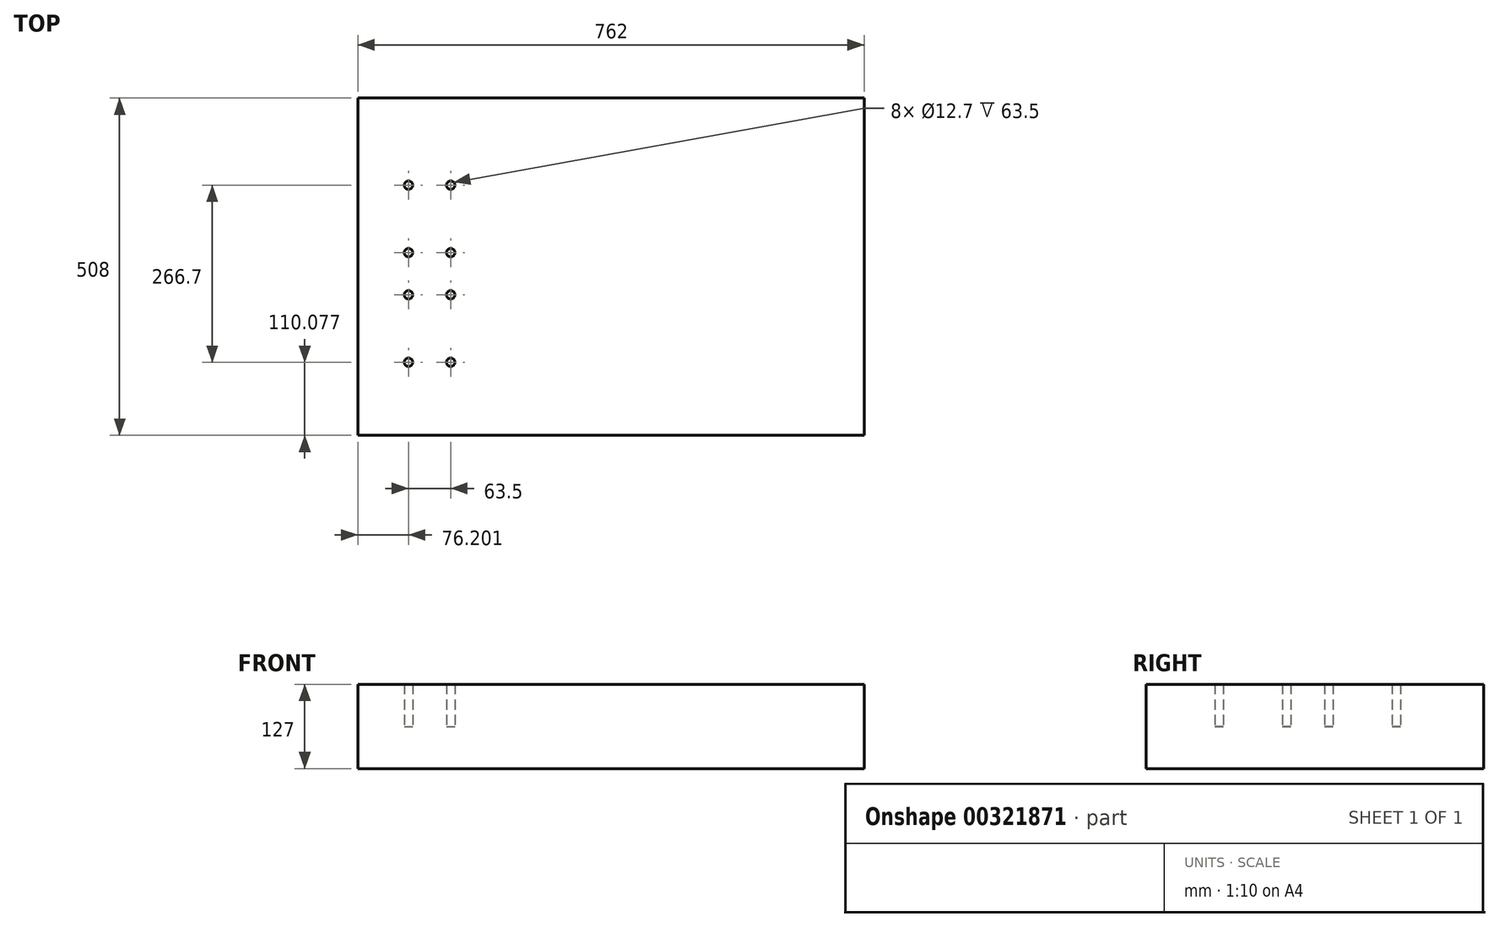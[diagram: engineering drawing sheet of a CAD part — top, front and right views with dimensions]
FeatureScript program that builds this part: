
annotation { "Feature Type Name" : "Feature", "Feature Type Description" : "" }
export const myFeature = defineFeature(function(context is Context, id is Id, definition is map)
    precondition{}
    {
        {
            var Q0;
            Q0=qCreatedBy(makeId("Top.planeOp"),FACE);
            var sketch = newSketch(context, id + "F0", { "sketchPlane" : qUnion([Q0])});
            skLineSegment(sketch, "E0.bottom", {"start": v(-379.12, 259.98) * mm, "end": v(382.88, 259.98) * mm});
            skLineSegment(sketch, "E0.top", {"start": v(-379.12, -248.02) * mm, "end": v(382.88, -248.02) * mm});
            skLineSegment(sketch, "E0.left", {"start": v(-379.12, 259.98) * mm, "end": v(-379.12, -248.02) * mm});
            skLineSegment(sketch, "E0.right", {"start": v(382.88, 259.98) * mm, "end": v(382.88, -248.02) * mm});
            skPoint(sketch, "E1", {"position": v(-302.92, 128.76) * mm});
            skPoint(sketch, "E2", {"position": v(-239.42, 128.76) * mm});
            skPoint(sketch, "E3", {"position": v(-302.92, -137.94) * mm});
            skPoint(sketch, "E4", {"position": v(-239.42, -137.94) * mm});
            skPoint(sketch, "E5", {"position": v(-302.92, -36.34) * mm});
            skPoint(sketch, "E6", {"position": v(-239.42, -36.34) * mm});
            skPoint(sketch, "E7", {"position": v(-302.92, 27.16) * mm});
            skPoint(sketch, "E8", {"position": v(-239.42, 27.16) * mm});
            skSolve(sketch);
        }
        {
            var Q0;
            Q0 = qSketchRegion(id + "F0", true);
            extrude(context, id + "F1", {"entities" : qUnion([Q0]), "endBound" : BoundingType.SYMMETRIC, "depth" : 127 * mm});
        }
        {
            var Q0;
            Q0=sQuery(id+"F0.wireOp",VERTEX,"E1");
            var Q1;
            Q1=sQuery(id+"F0.wireOp",VERTEX,"E2");
            var Q2;
            Q2=sQuery(id+"F0.wireOp",VERTEX,"E7");
            var Q3;
            Q3=sQuery(id+"F0.wireOp",VERTEX,"E8");
            var Q4;
            Q4=sQuery(id+"F0.wireOp",VERTEX,"E5");
            var Q5;
            Q5=sQuery(id+"F0.wireOp",VERTEX,"E6");
            var Q6;
            Q6=sQuery(id+"F0.wireOp",VERTEX,"E3");
            var Q7;
            Q7=sQuery(id+"F0.wireOp",VERTEX,"E4");
            var Q8;
            Q8=makeQuery(id+"F1.opExtrude","SWEPT_BODY",BODY,{"disambiguationData":[OSD([sQuery(id+"F0.wireOp",EDGE,"E0.bottom"),sQuery(id+"F0.wireOp",EDGE,"E0.top"),sQuery(id+"F0.wireOp",EDGE,"E0.left"),sQuery(id+"F0.wireOp",EDGE,"E0.right")])]});
            hole(context, id + "F2", {"style" : HoleStyle.SIMPLE, "endStyle" : HoleEndStyle.THROUGH, "oppositeDirection" : true, "holeDiameter" : 12.7 * mm, "tappedDepth" : 12.7 * mm, "tapClearance" : 3, "locations" : qUnion([Q0, Q1, Q2, Q3, Q4, Q5, Q6, Q7]), "scope" : qUnion([Q8])});
        }
    });
